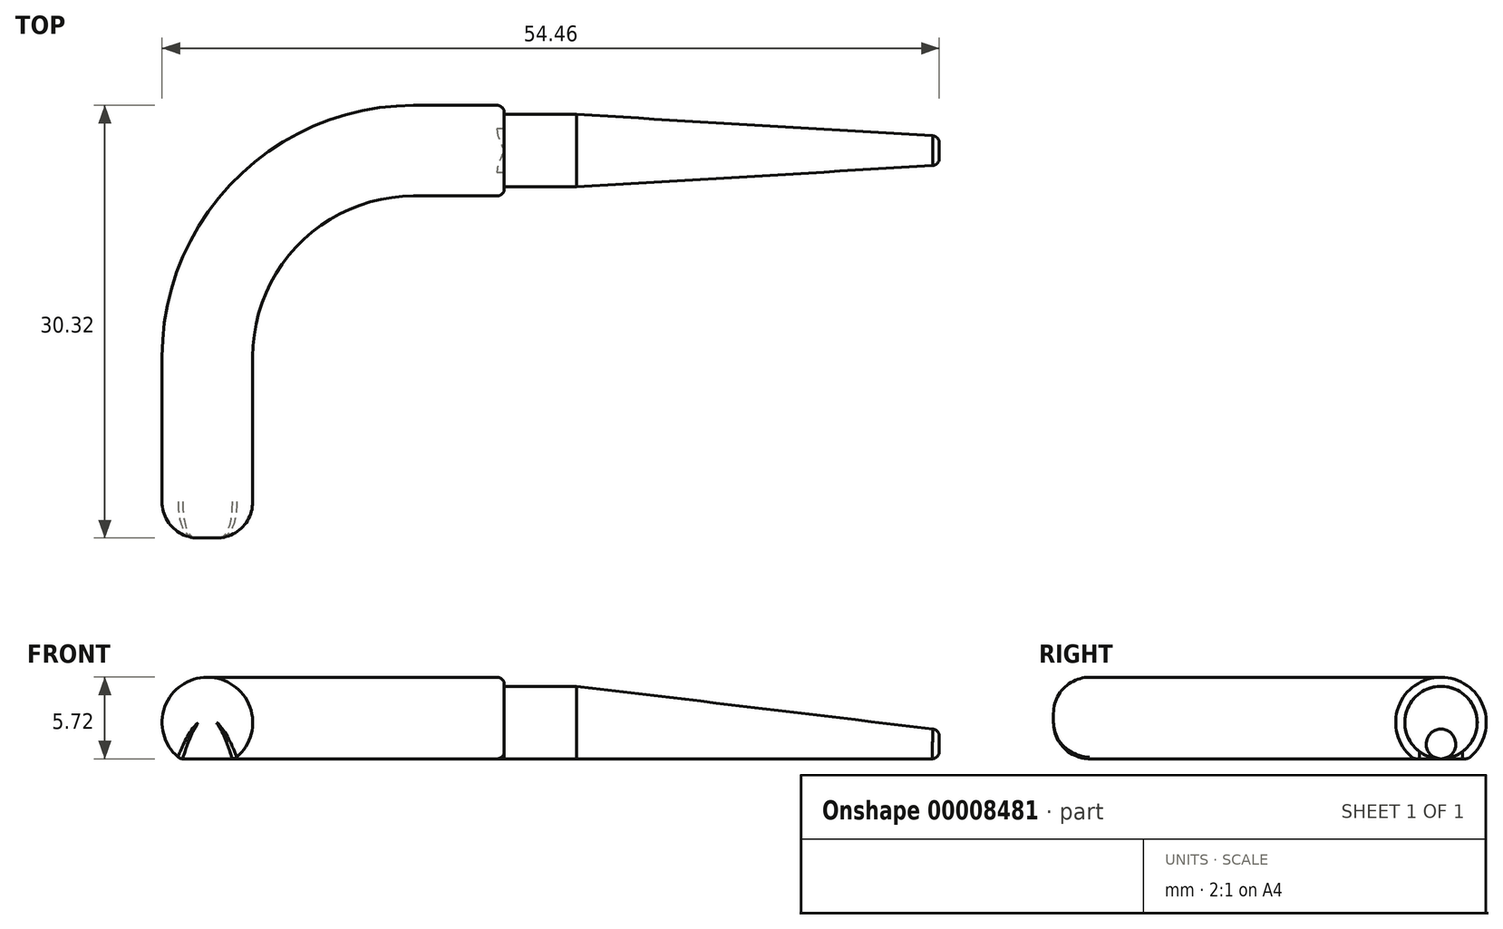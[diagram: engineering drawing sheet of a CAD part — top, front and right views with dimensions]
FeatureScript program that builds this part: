
annotation { "Feature Type Name" : "Feature", "Feature Type Description" : "" }
export const myFeature = defineFeature(function(context is Context, id is Id, definition is map)
    precondition{}
    {
        {
            var Q0;
            Q0=qCreatedBy(makeId("Right.planeOp"),FACE);
            var sketch = newSketch(context, id + "F0", { "sketchPlane" : qUnion([Q0])});
            skCircle(sketch, "E0", {"center": v(0, 1.02) * mm, "radius": 1.02 * mm});
            skLineSegment(sketch, "E1", {"start": v(0, 0) * mm, "end": v(0, 1.02) * mm});
            skSolve(sketch);
        }
        {
            var Q0;
            Q0=qCreatedBy(makeId("Right.planeOp"),FACE);
            cPlane(context, id + "F1", {"entities" : qUnion([Q0]), "cplaneType" : CPlaneType.OFFSET, "offset" : 25.4 * mm, "oppositeDirection" : true, "width" : 152.4 * mm, "height" : 152.4 * mm});
        }
        {
            var Q0;
            Q0=qCreatedBy(id+"F1.planeOp",FACE);
            var sketch = newSketch(context, id + "F2", { "sketchPlane" : qUnion([Q0])});
            skCircle(sketch, "E2.0", {"center": v(0, 1.02) * mm, "radius": 1.02 * mm, "construction": true});
            skCircle(sketch, "E3", {"center": v(0, 2.54) * mm, "radius": 2.54 * mm});
            skLineSegment(sketch, "E4", {"start": v(0, 2.54) * mm, "end": v(0, 1.02) * mm, "construction": true});
            skSolve(sketch);
        }
        {
            var Q0;
            Q0=makeQuery(id+"F0.imprint","IMPRINT",FACE,{"disambiguationData":[TD([[makeQuery(id+"F0.imprint","IMPRINT",EDGE,{"derivedFrom":sQuery(id+"F0.wireOp",EDGE,"E0")}),1.0]])]});
            var Q1;
            Q1=makeQuery(id+"F2.imprint","IMPRINT",FACE,{"disambiguationData":[TD([[makeQuery(id+"F2.imprint","IMPRINT",EDGE,{"derivedFrom":sQuery(id+"F2.wireOp",EDGE,"E3")}),1.0]])]});
            loft(context, id + "F3", {"sheetProfilesArray" : [{ "sheetProfileEntities" : qUnion([Q0]) }, { "sheetProfileEntities" : qUnion([Q1]) }]});
        }
        {
            var Q0;
            Q0=makeQuery(id+"F3.opLoft","CAP_FACE",FACE,{"disambiguationData":[OSD([makeQuery(id+"F2.imprint","IMPRINT",FACE,{"disambiguationData":[TD([[makeQuery(id+"F2.imprint","IMPRINT",EDGE,{"derivedFrom":sQuery(id+"F2.wireOp",EDGE,"E3")}),1.0]])]})])],"isStart":true});
            extrude(context, id + "F4", {"entities" : qUnion([Q0]), "operationType" : NewBodyOperationType.ADD, "depth" : 5.08 * mm});
        }
        {
            var Q0;
            Q0=makeQuery(id+"F4.opExtrude","CAP_FACE",FACE,{"disambiguationData":[OSD([makeQuery(id+"F2.imprint","IMPRINT",FACE,{"disambiguationData":[TD([[makeQuery(id+"F2.imprint","IMPRINT",EDGE,{"derivedFrom":sQuery(id+"F2.wireOp",EDGE,"E3")}),1.0]])]})])],"isStart":false});
            var sketch = newSketch(context, id + "F5", { "sketchPlane" : qUnion([Q0])});
            skCircle(sketch, "E5", {"center": v(0, 2.54) * mm, "radius": 3.18 * mm});
            skLineSegment(sketch, "E6", {"start": v(0, 5.08) * mm, "end": v(0, 0) * mm, "construction": true});
            skLineSegment(sketch, "E7", {"start": v(0, 0) * mm, "end": v(1.9, 0) * mm});
            skLineSegment(sketch, "E8", {"start": v(0, 0) * mm, "end": v(-1.9, 0) * mm});
            skSolve(sketch);
        }
        {
            var Q0;
            {var subQ1=sQuery(id+"F5.wireOp",EDGE,"E7");Q0=makeQuery(id+"F5.imprint","IMPRINT",FACE,{"disambiguationData":[TD([[makeQuery(id+"F5.imprint","IMPRINT",EDGE,{"derivedFrom":subQ1}),1.0]])]});}
            var Q1;
            Q1=makeQuery(id+"F5.imprint","IMPRINT",FACE,{"disambiguationData":[TD([[makeQuery(id+"F5.imprint","IMPRINT",EDGE,{"derivedFrom":makeQuery(id+"F4.opExtrude","CAP_EDGE",EDGE,{"disambiguationData":[OSD([sQuery(id+"F0.wireOp",EDGE,"E0"),sQuery(id+"F2.wireOp",EDGE,"E3")])],"isStart":false})}),1.0]])]});
            extrude(context, id + "F6", {"entities" : qUnion([Q0, Q1]), "operationType" : NewBodyOperationType.ADD, "depth" : 6.35 * mm});
        }
        {
            var Q0;
            Q0=makeQuery(id+"F6.opExtrude","SWEPT_FACE",FACE,{"disambiguationData":[OSD([sQuery(id+"F5.wireOp",EDGE,"E7"),sQuery(id+"F5.wireOp",EDGE,"E8")])]});
            var sketch = newSketch(context, id + "F7", { "sketchPlane" : qUnion([Q0])});
            skArc(sketch, "E9", {"start": v(-49.38, 14.45) * mm, "mid": v(-45.7, 5.58) * mm, "end": v(-36.83, 1.9) * mm});
            skLineSegment(sketch, "E10", {"start": v(-36.83, 1.9) * mm, "end": v(-36.83, 14.45) * mm, "construction": true});
            skLineSegment(sketch, "E11", {"start": v(-36.83, 14.45) * mm, "end": v(-49.38, 14.45) * mm, "construction": true});
            skSolve(sketch);
        }
        {
            var Q0;
            Q0=makeQuery(id+"F6.opExtrude","CAP_FACE",FACE,{"disambiguationData":[OSD([sQuery(id+"F5.wireOp",EDGE,"E5"),sQuery(id+"F5.wireOp",EDGE,"E7"),sQuery(id+"F5.wireOp",EDGE,"E8")])],"isStart":false});
            var Q1;
            Q1=sQuery(id+"F7.wireOp",EDGE,"E9");
            sweep(context, id + "F8", {"operationType" : NewBodyOperationType.ADD, "profiles" : qUnion([Q0]), "path" : qUnion([Q1])});
        }
        {
            var Q0;
            Q0=makeQuery(id+"F8.opSweep","CAP_FACE",FACE,{"disambiguationData":[OSD([sQuery(id+"F5.wireOp",EDGE,"E5"),sQuery(id+"F5.wireOp",EDGE,"E7"),sQuery(id+"F5.wireOp",EDGE,"E8"),sQuery(id+"F7.wireOp",VERTEX,"E9.start")])],"isStart":false});
            extrude(context, id + "F9", {"entities" : qUnion([Q0]), "operationType" : NewBodyOperationType.ADD, "depth" : 12.7 * mm});
        }
        {
            var Q0;
            Q0=makeQuery(id+"F9.opExtrude","CAP_FACE",FACE,{"disambiguationData":[OSD([sQuery(id+"F5.wireOp",EDGE,"E5"),sQuery(id+"F5.wireOp",EDGE,"E7"),sQuery(id+"F5.wireOp",EDGE,"E8"),sQuery(id+"F7.wireOp",VERTEX,"E9.start")])],"isStart":false});
            fillet(context, id + "F10", {"entities" : qUnion([Q0]), "radius" : 2.54 * mm, "tangentPropagation" : true, "allowEdgeOverflow" : false});
        }
        {
            var Q0;
            Q0=makeQuery(id+"F3.opLoft","MID_CAP_EDGE",EDGE,{"disambiguationData":[OSD([sQuery(id+"F0.wireOp",EDGE,"E0")])],"capPos":0.0});
            var Q1;
            Q1=makeQuery(id+"F6.opExtrude","CAP_EDGE",EDGE,{"disambiguationData":[OSD([sQuery(id+"F5.wireOp",EDGE,"E5")])],"isStart":true});
            var Q2;
            {var subQ0=sQuery(id+"F5.wireOp",EDGE,"E7");var subQ1=sQuery(id+"F5.wireOp",EDGE,"E8");Q2=makeQuery(id+"F9.boolean.opBoolean","MERGE",FACE,{"derivedFrom":[makeQuery(id+"F8.boolean.opBoolean","MERGE",FACE,{"derivedFrom":[makeQuery(id+"F6.opExtrude","SWEPT_FACE",FACE,{"disambiguationData":[OSD([subQ0,subQ1])]}),makeQuery(id+"F8.opSweep","SWEPT_FACE",FACE,{"disambiguationData":[OSD([subQ0,subQ1,sQuery(id+"F7.wireOp",EDGE,"E9")])]})]}),makeQuery(id+"F9.opExtrude","SWEPT_FACE",FACE,{"disambiguationData":[OSD([subQ0,subQ1,sQuery(id+"F7.wireOp",VERTEX,"E9.start")])]})]});}
            var Q3;
            Q3=makeQuery(id+"F10.opFillet","BLEND_FACE",FACE,{"disambiguationData":[OSD([sQuery(id+"F5.wireOp",EDGE,"E7"),sQuery(id+"F5.wireOp",EDGE,"E8"),sQuery(id+"F7.wireOp",VERTEX,"E9.start")])]});
            fillet(context, id + "F11", {"entities" : qUnion([Q0, Q1, Q2, Q3]), "radius" : 0.5 * mm, "tangentPropagation" : true, "allowEdgeOverflow" : false});
        }
    });
